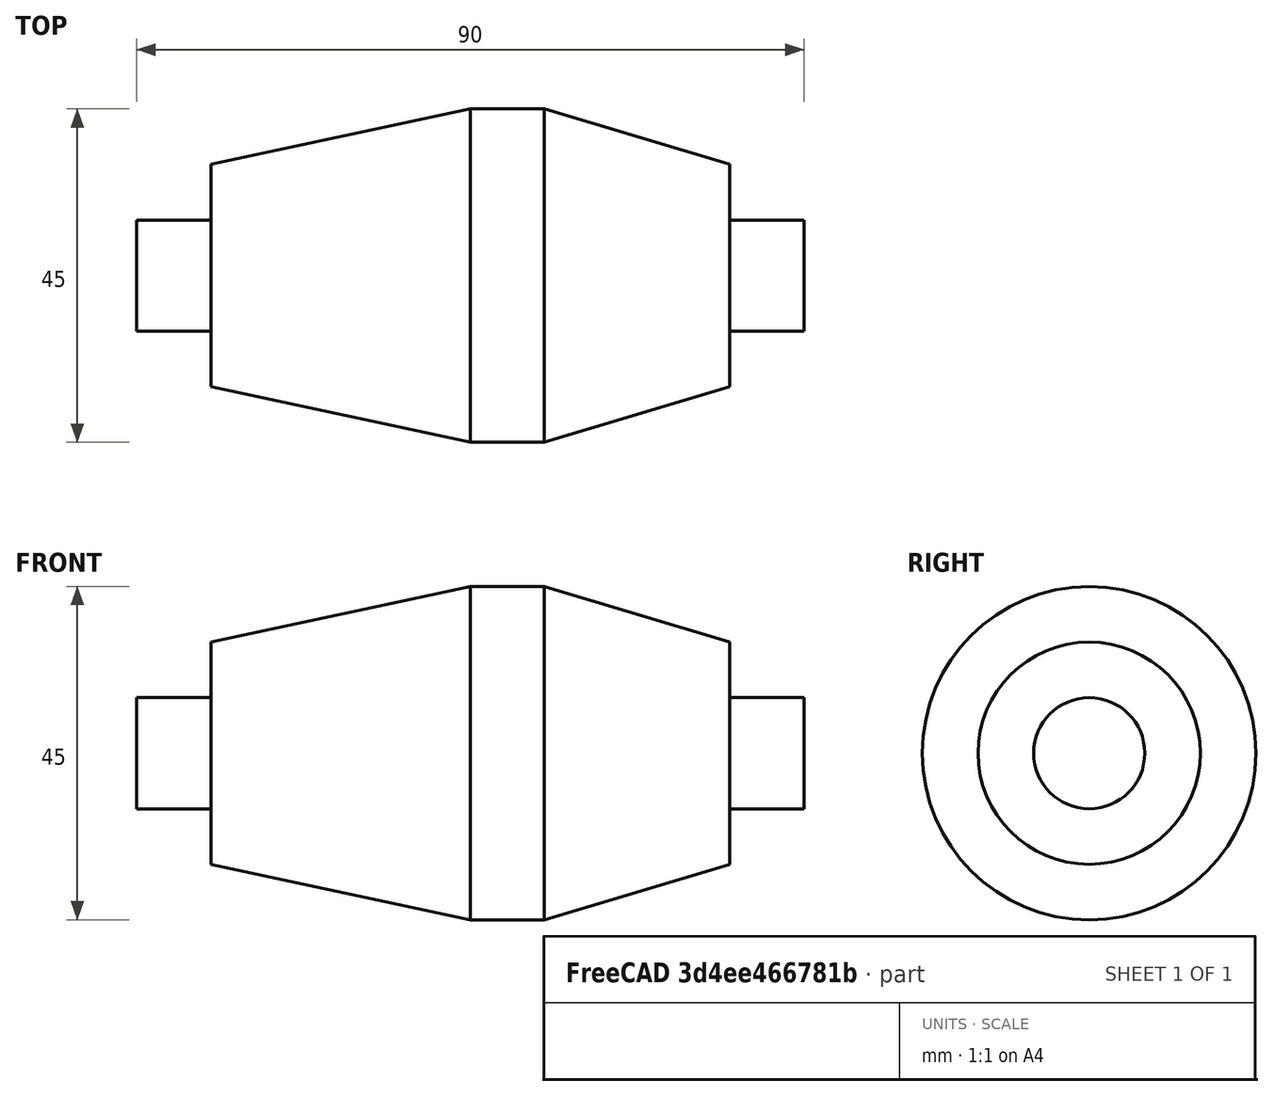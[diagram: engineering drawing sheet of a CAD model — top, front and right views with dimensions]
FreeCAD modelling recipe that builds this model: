
FCSTD DOCUMENT  (FreeCAD 0.19R)
Label: drum
License: All rights reserved
LicenseURL: http://en.wikipedia.org/wiki/All_rights_reserved
objects: Sketcher::SketchObject×1, PartDesign::Revolution×1, PartDesign::Body×1
note: 4 computed .brp shape members not serialized (recipe doc carries the construction recipe); baked Part::Feature solids carry a one-line shape summary decoded from their .brp

FEATURE [Sketcher::SketchObject] Sketch
  MapMode = 5
  Support = -> [XY_Plane]
  sketch-geometry (10):
    g0: LineSegment StartX=0 StartY=0 StartZ=0 EndX=0 EndY=7.5 EndZ=0
    g1: LineSegment StartX=0 StartY=7.5 StartZ=0 EndX=10 EndY=7.5 EndZ=0
    g2: LineSegment StartX=10 StartY=7.5 StartZ=0 EndX=10 EndY=15 EndZ=0
    g3: LineSegment StartX=10 StartY=15 StartZ=0 EndX=45 EndY=22.5 EndZ=0
    g4: LineSegment StartX=45 StartY=22.5 StartZ=0 EndX=55 EndY=22.5 EndZ=0
    g5: LineSegment StartX=55 StartY=22.5 StartZ=0 EndX=80 EndY=15 EndZ=0
    g6: LineSegment StartX=80 StartY=15 StartZ=0 EndX=80 EndY=7.5 EndZ=0
    g7: LineSegment StartX=80 StartY=7.5 StartZ=0 EndX=90 EndY=7.5 EndZ=0
    g8: LineSegment StartX=90 StartY=7.5 StartZ=0 EndX=90 EndY=0 EndZ=0
    g9: LineSegment StartX=90 StartY=0 StartZ=0 EndX=0 EndY=0 EndZ=0
  constraints (29):
    c: Coincident(g0,g-1)
    c: PointOnObject(g0,g-2)
    c: Coincident(g1,g0)
    c: Horizontal(g1)
    c: Coincident(g2,g1)
    c: Vertical(g2)
    c: Coincident(g3,g2)
    c: Coincident(g4,g3)
    c: Horizontal(g4)
    c: Coincident(g5,g4)
    c: Coincident(g6,g5)
    c: Vertical(g6)
    c: Coincident(g7,g6)
    c: Horizontal(g7)
    c: Coincident(g8,g7)
    c: PointOnObject(g8,g-1)
    c: Vertical(g8)
    c: Coincident(g9,g8)
    c: Coincident(g9,g0)
    c: DistanceY(g0,g0) = 7.5
    c: Equal(g8,g0)
    c: Equal(g1,g7)
    c: DistanceX(g1,g1) = 10
    c: DistanceY(g0,g2) = 15
    c: Equal(g6,g2)
    c: DistanceY(g0,g3) = 22.5
    c: DistanceX(g4,g4) = 10
    c: DistanceX(g2,g3) = 35
    c: DistanceX(g4,g5) = 25
FEATURE [PartDesign::Revolution] Revolution
  Angle = 360
  Axis = (1,0,0)
  Base = (0,0,0)
  Profile = -> Sketch
  ReferenceAxis = -> X_Axis
  Reversed = true
FEATURE [PartDesign::Body] Body
  Group = -> [Sketch,Revolution]
  Origin = -> Origin
  Tip = -> Revolution
